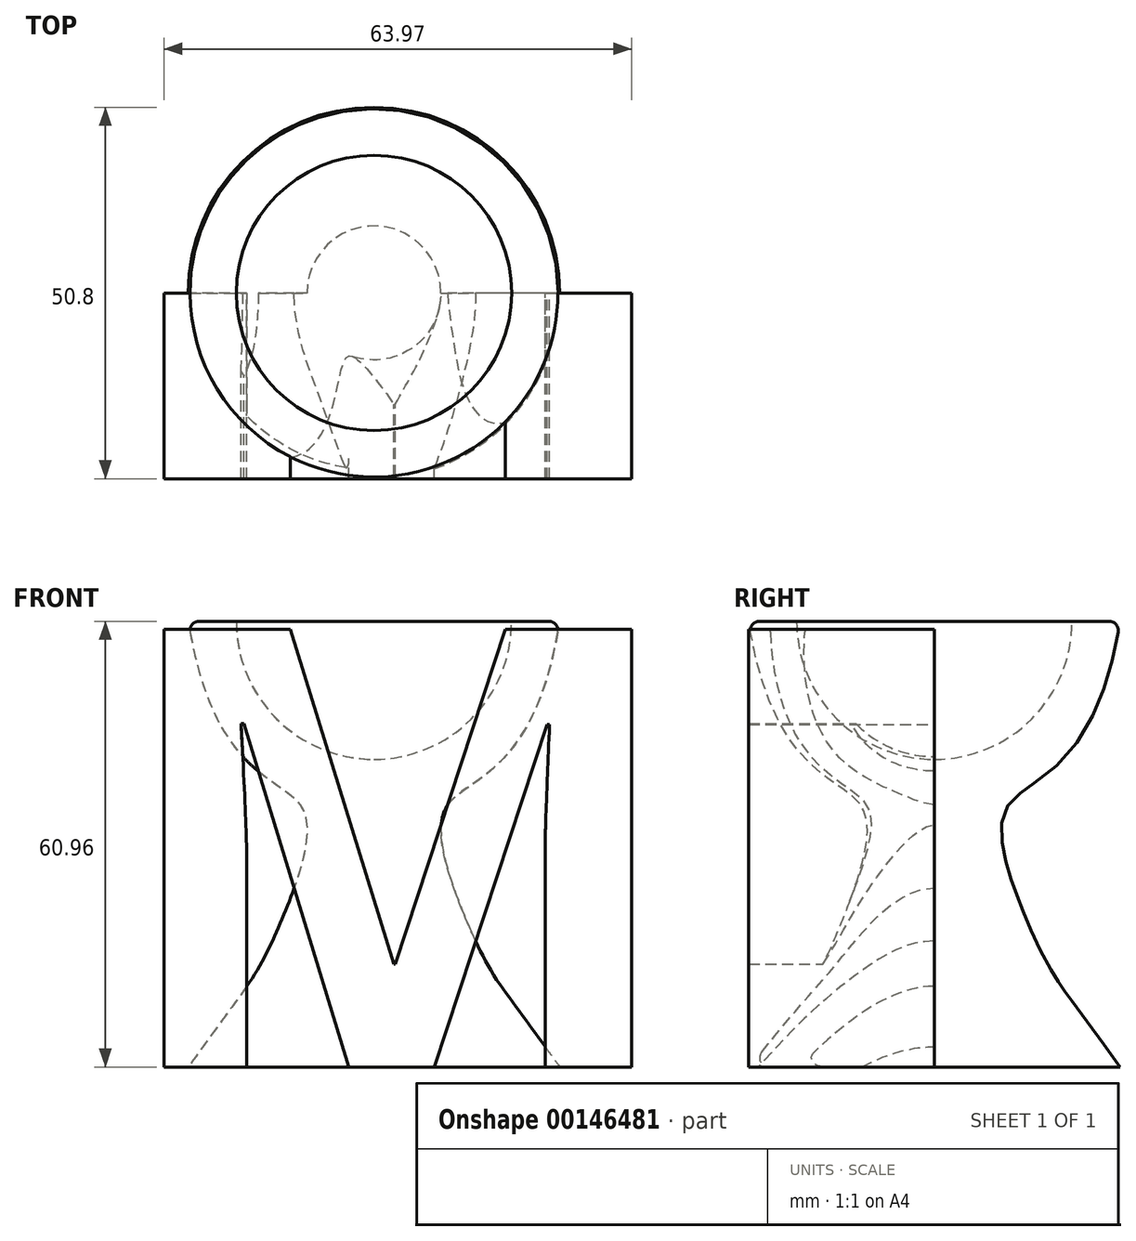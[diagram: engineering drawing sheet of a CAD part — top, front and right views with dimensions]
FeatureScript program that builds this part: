
annotation { "Feature Type Name" : "Feature", "Feature Type Description" : "" }
export const myFeature = defineFeature(function(context is Context, id is Id, definition is map)
    precondition{}
    {
        {
            var Q0;
            Q0=qCreatedBy(makeId("Top.planeOp"),FACE);
            var sketch = newSketch(context, id + "F0", { "sketchPlane" : qUnion([Q0])});
            skCircle(sketch, "E0", {"center": v(0, 0) * mm, "radius": 25.4 * mm});
            skSolve(sketch);
        }
        {
            var Q0;
            Q0 = qSketchRegion(id + "F0", true);
            extrude(context, id + "F1", {"entities" : qUnion([Q0]), "depth" : 60.96 * mm});
        }
        {
            var Q0;
            Q0=qCreatedBy(makeId("Right.planeOp"),FACE);
            var sketch = newSketch(context, id + "F2", { "sketchPlane" : qUnion([Q0])});
            skLineSegment(sketch, "E1", {"start": v(-25.4, 68.38) * mm, "end": v(-25.4, -13.01) * mm});
            skLineSegment(sketch, "E2", {"start": v(0, 73.92) * mm, "end": v(0, -13.01) * mm, "construction": true});
            skLineSegment(sketch, "E3", {"start": v(-57.59, 60.96) * mm, "end": v(44.57, 60.96) * mm, "construction": true});
            skFitSpline(sketch, "E4", {"points": [v(-25.4, 60.96) * mm, v(-9.69, 35.16) * mm, v(-11.9, 21.87) * mm, v(-15.78, 13.57) * mm, v(-25.4, 0) * mm], "startDerivative": vector(31.04, -196.06) * mm, "endDerivative": vector(-78.7, -109.36) * mm});
            skLineSegment(sketch, "E5", {"start": v(-25.4, 60.96) * mm, "end": v(-25.4, 0) * mm});
            skSolve(sketch);
        }
        {
            var Q0;
            Q0 = qSketchRegion(id + "F2", true);
            var Q1;
            Q1=sQuery(id+"F2.wireOp",EDGE,"E2");
            revolve(context, id + "F3", {"operationType" : NewBodyOperationType.REMOVE, "entities" : qUnion([Q0]), "axis" : qUnion([Q1]), "revolveType" : RevolveType.FULL, "oppositeDirection" : true});
        }
        {
            var Q0;
            Q0=qCreatedBy(makeId("Front.planeOp"),FACE);
            var sketch = newSketch(context, id + "F4", { "sketchPlane" : qUnion([Q0])});
            skText(sketch, "E6", { "text": "M", "fontName": "OpenSans-Bold.ttf"});
            const initialGuessF4  = {"E6": [-0.03627, 0, 1, 0, 0.06035]};
            skSetInitialGuess(sketch, initialGuessF4);
            skSolve(sketch);
        }
        {
            var Q0;
            Q0 = qSketchRegion(id + "F4", true);
            extrude(context, id + "F5", {"entities" : qUnion([Q0]), "operationType" : NewBodyOperationType.ADD, "depth" : 25.4 * mm});
        }
        {
            var Q0;
            Q0=qCreatedBy(makeId("Front.planeOp"),FACE);
            var sketch = newSketch(context, id + "F6", { "sketchPlane" : qUnion([Q0])});
            skArc(sketch, "E7", {"start": v(0, 42.08) * mm, "mid": v(18.83, 60.9) * mm, "end": v(0, 79.73) * mm});
            skLineSegment(sketch, "E8", {"start": v(0, 79.73) * mm, "end": v(0, 42.08) * mm});
            skSolve(sketch);
        }
        {
            var Q0;
            Q0 = qSketchRegion(id + "F6", true);
            var Q1;
            Q1=sQuery(id+"F6.wireOp",EDGE,"E8");
            revolve(context, id + "F7", {"operationType" : NewBodyOperationType.REMOVE, "entities" : qUnion([Q0]), "axis" : qUnion([Q1]), "revolveType" : RevolveType.FULL, "oppositeDirection" : true});
        }
        {
            var Q0;
            {var subQ0=sQuery(id+"F2.wireOp",EDGE,"E5");var subQ1=sQuery(id+"F2.wireOp",EDGE,"E4");Q0=makeQuery(id+"F3.boolean.opBoolean","MERGE",EDGE,{"derivedFrom":[makeQuery(id+"F1.opExtrude","CAP_EDGE",EDGE,{"disambiguationData":[OSD([sQuery(id+"F0.wireOp",EDGE,"E0")])],"isStart":false}),makeQuery(id+"F3.opRevolve","SWEPT_EDGE",EDGE,{"disambiguationData":[OSD([subQ1,subQ0]),TDD([makeQuery(id+"F2.imprint","INTERSECT",VERTEX,{"disambiguationData":[OD(0.0)],"derivedFrom":[subQ1,subQ0]})])]})]});}
            var Q1;
            {var subQ0=sQuery(id+"F2.wireOp",EDGE,"E4");var subQ1=sQuery(id+"F0.wireOp",EDGE,"E0");var subQ2=sQuery(id+"F2.wireOp",EDGE,"E5");Q1=makeQuery(id+"F5.boolean.opBoolean","SPLIT",EDGE,{"disambiguationData":[TD([makeQuery(id+"F5.opExtrude","SWEPT_FACE",FACE,{"disambiguationData":[OSD([sQuery(id+"F4.wireOp",EDGE,"E6.sketch_text.stroke-0")])]})])],"derivedFrom":makeQuery(id+"F3.boolean.opBoolean","MERGE",EDGE,{"derivedFrom":[makeQuery(id+"F1.opExtrude","CAP_EDGE",EDGE,{"disambiguationData":[OSD([subQ1])],"isStart":true}),makeQuery(id+"F3.opRevolve","SWEPT_EDGE",EDGE,{"disambiguationData":[OSD([subQ0,subQ2]),TDD([makeQuery(id+"F2.imprint","INTERSECT",VERTEX,{"disambiguationData":[OD(1.0)],"derivedFrom":[subQ0,subQ2]})])]})]})});}
            fillet(context, id + "F8", {"entities" : qUnion([Q0, Q1]), "radius" : 1.27 * mm, "tangentPropagation" : true, "allowEdgeOverflow" : false});
        }
    });
